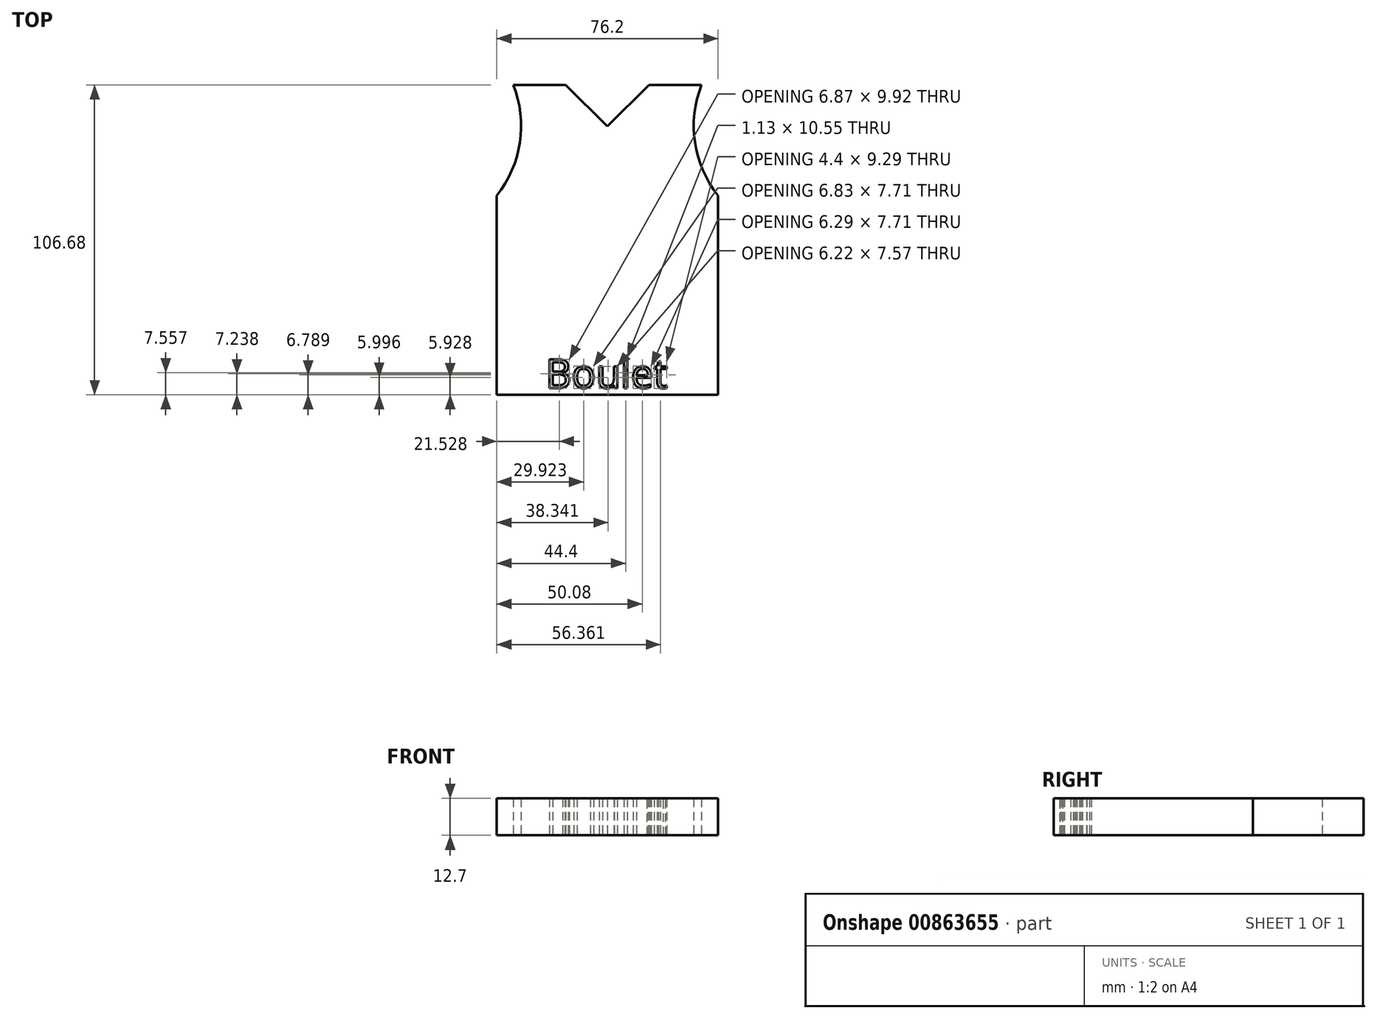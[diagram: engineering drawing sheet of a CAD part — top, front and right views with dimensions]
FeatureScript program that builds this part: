
annotation { "Feature Type Name" : "Feature", "Feature Type Description" : "" }
export const myFeature = defineFeature(function(context is Context, id is Id, definition is map)
    precondition{}
    {
        {
            var Q0;
            Q0=qCreatedBy(makeId("Top.planeOp"),FACE);
            var sketch = newSketch(context, id + "F0", { "sketchPlane" : qUnion([Q0])});
            skLineSegment(sketch, "E0", {"start": v(-38.1, -68.58) * mm, "end": v(0, -68.58) * mm});
            skLineSegment(sketch, "E1.MirrorCS", {"start": v(38.1, -68.58) * mm, "end": v(0, -68.58) * mm});
            skPoint(sketch, "E2.visualSharp", {"position": v(0, 23.82) * mm});
            skLineSegment(sketch, "E3", {"start": v(38.1, -68.58) * mm, "end": v(38.1, 0) * mm});
            skLineSegment(sketch, "E4.MirrorCS", {"start": v(-38.1, -68.58) * mm, "end": v(-38.1, 0) * mm});
            skLineSegment(sketch, "E5", {"start": v(-32.4, 38.1) * mm, "end": v(-14.35, 38.1) * mm});
            skLineSegment(sketch, "E6", {"start": v(-14.35, 38.1) * mm, "end": v(0, 23.82) * mm});
            skLineSegment(sketch, "E7.MirrorCS", {"start": v(14.35, 38.1) * mm, "end": v(0, 23.82) * mm});
            skLineSegment(sketch, "E8.MirrorCS", {"start": v(32.4, 38.1) * mm, "end": v(14.35, 38.1) * mm});
            skArc(sketch, "E9", {"start": v(32.4, 38.1) * mm, "mid": v(30.13, 18.28) * mm, "end": v(38.1, 0) * mm});
            skArc(sketch, "E10.MirrorCS", {"start": v(-32.4, 38.1) * mm, "mid": v(-30.13, 18.28) * mm, "end": v(-38.1, 0) * mm});
            skLineSegment(sketch, "E11", {"start": v(-18.65, 38.1) * mm, "end": v(0, 19.54) * mm});
            skLineSegment(sketch, "E12", {"start": v(0, 19.54) * mm, "end": v(18.65, 38.1) * mm});
            skArc(sketch, "E13", {"start": v(29.35, 38.1) * mm, "mid": v(27.6, 16.22) * mm, "end": v(38.1, -3.05) * mm});
            skArc(sketch, "E14.MirrorCS", {"start": v(-29.35, 38.1) * mm, "mid": v(-27.6, 16.22) * mm, "end": v(-38.1, -3.05) * mm});
            skSolve(sketch);
        }
        {
            var Q0;
            Q0 = qSketchRegion(id + "F0", true);
            extrude(context, id + "F1", {"entities" : qUnion([Q0]), "depth" : 12.7 * mm, "offsetDistance" : 25.4 * mm});
        }
        {
            var Q0;
            Q0=qCreatedBy(makeId("Top.planeOp"),FACE);
            var sketch = newSketch(context, id + "F2", { "sketchPlane" : qUnion([Q0])});
            skText(sketch, "E15", { "text": "Boulet\n", "fontName": "OpenSans-Regular.ttf"});
            const initialGuessF2  = {"E15": [-0.02137, -0.0663, 1, 0, 0.01]};
            skSetInitialGuess(sketch, initialGuessF2);
            skSolve(sketch);
        }
        {
            var Q0;
            Q0 = qSketchRegion(id + "F2", true);
            extrude(context, id + "F3", {"entities" : qUnion([Q0]), "operationType" : NewBodyOperationType.REMOVE, "depth" : 12.7 * mm, "offsetDistance" : 25.4 * mm});
        }
        {
            var Q0;
            Q0=qCreatedBy(makeId("Top.planeOp"),FACE);
            var sketch = newSketch(context, id + "F4", { "sketchPlane" : qUnion([Q0])});
            skText(sketch, "E16", { "text": "4\n", "fontName": "OpenSans-Regular.ttf"});
            const initialGuessF4  = {"E16": [-0.01833, -0.04448, 1, 0, 0.04282]};
            skSetInitialGuess(sketch, initialGuessF4);
            skSolve(sketch);
        }
        {
            var Q0;
            Q0 = qSketchRegion(id + "F4", true);
            extrude(context, id + "F5", {"entities" : qUnion([Q0]), "operationType" : NewBodyOperationType.REMOVE, "oppositeDirection" : true, "depth" : 12.7 * mm, "offsetDistance" : 25.4 * mm});
        }
    });
